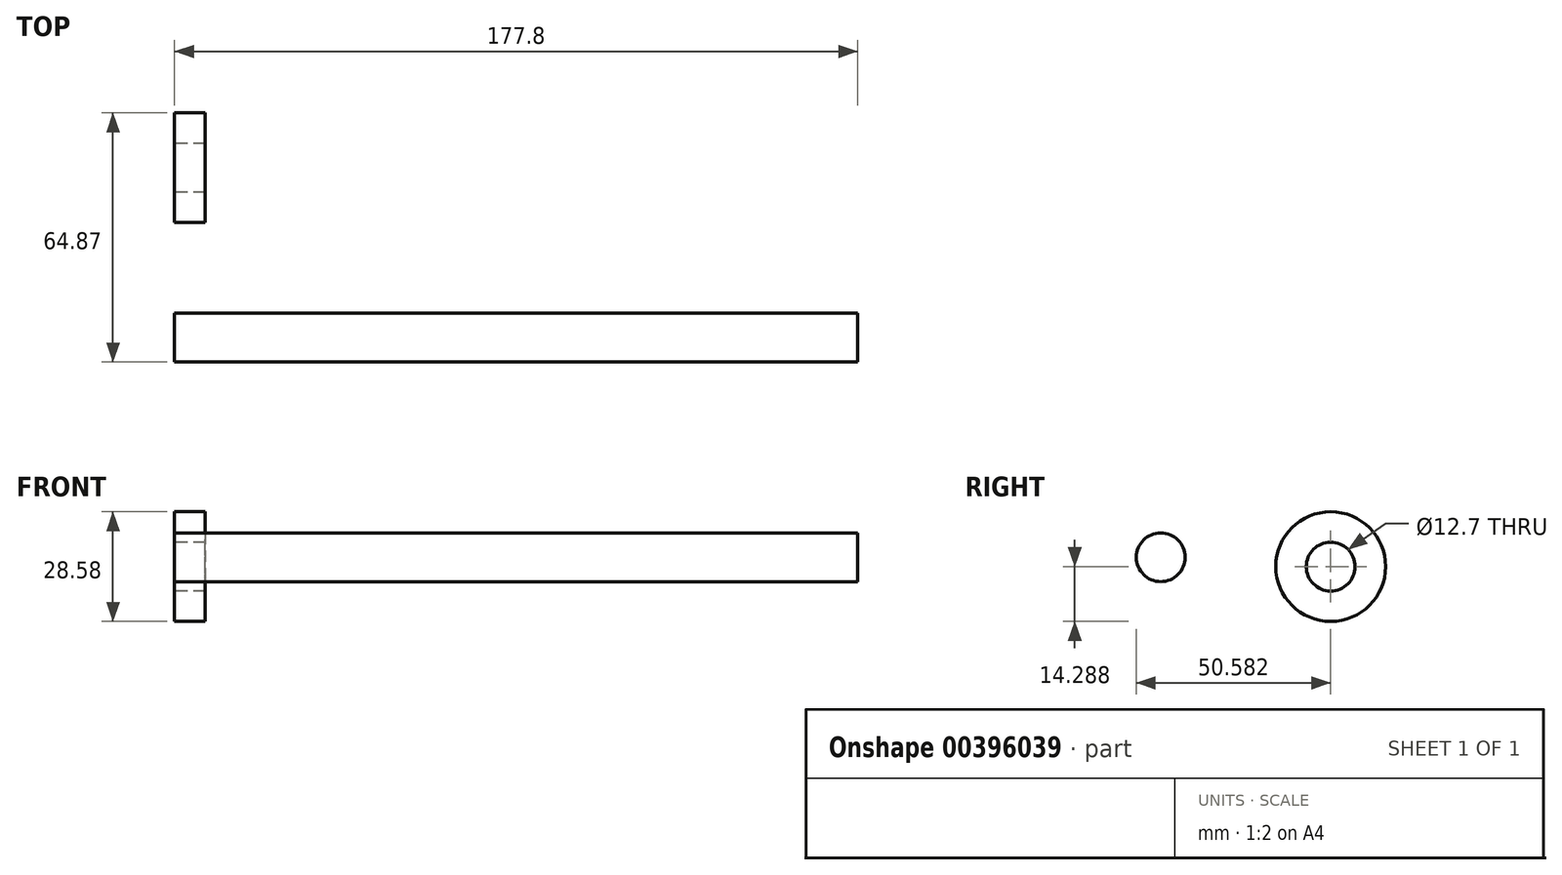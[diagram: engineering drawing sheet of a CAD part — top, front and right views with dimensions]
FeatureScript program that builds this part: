
annotation { "Feature Type Name" : "Feature", "Feature Type Description" : "" }
export const myFeature = defineFeature(function(context is Context, id is Id, definition is map)
    precondition{}
    {
        {
            var Q0;
            Q0=qCreatedBy(makeId("Right.planeOp"),FACE);
            var sketch = newSketch(context, id + "F0", { "sketchPlane" : qUnion([Q0])});
            skCircle(sketch, "E0", {"center": v(-15.34, 32.9) * mm, "radius": 6.35 * mm});
            skSolve(sketch);
        }
        {
            var Q0;
            Q0=makeQuery(id+"F0.imprint","IMPRINT",FACE,{"disambiguationData":[TD([[makeQuery(id+"F0.imprint","IMPRINT",EDGE,{"derivedFrom":sQuery(id+"F0.wireOp",EDGE,"E0")}),1.0]])]});
            extrude(context, id + "F1", {"entities" : qUnion([Q0]), "offsetDistance" : 25.4 * mm, "depth" : 177.8 * mm});
        }
        {
            var Q0;
            Q0=qCreatedBy(makeId("Right.planeOp"),FACE);
            var sketch = newSketch(context, id + "F2", { "sketchPlane" : qUnion([Q0])});
            skCircle(sketch, "E1", {"center": v(28.9, 30.45) * mm, "radius": 6.35 * mm});
            skCircle(sketch, "E2", {"center": v(28.9, 30.45) * mm, "radius": 14.29 * mm});
            skSolve(sketch);
        }
        {
            var Q0;
            Q0=makeQuery(id+"F2.imprint","IMPRINT",FACE,{"disambiguationData":[TD([[makeQuery(id+"F2.imprint","IMPRINT",EDGE,{"derivedFrom":sQuery(id+"F2.wireOp",EDGE,"E1")}),-1.0]])]});
            extrude(context, id + "F3", {"entities" : qUnion([Q0]), "depth" : 7.92 * mm});
        }
    });
